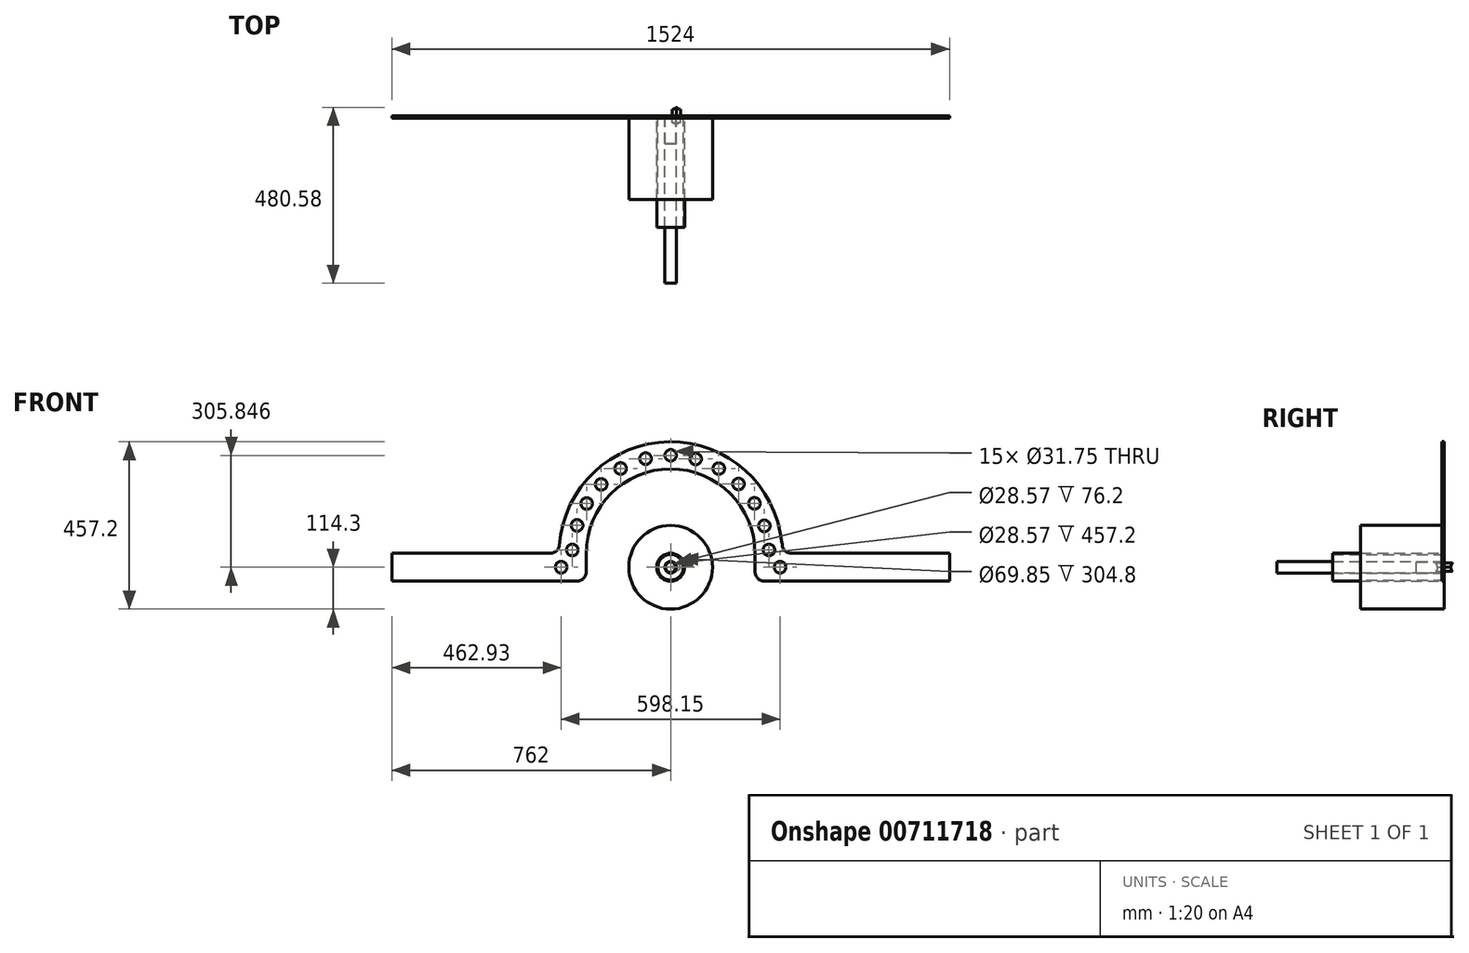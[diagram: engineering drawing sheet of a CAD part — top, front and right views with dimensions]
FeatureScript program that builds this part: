
annotation { "Feature Type Name" : "Feature", "Feature Type Description" : "" }
export const myFeature = defineFeature(function(context is Context, id is Id, definition is map)
    precondition{}
    {
        {
            var Q0;
            Q0=qCreatedBy(makeId("Front.planeOp"),FACE);
            var sketch = newSketch(context, id + "F0", { "sketchPlane" : qUnion([Q0])});
            skLineSegment(sketch, "E0.top", {"start": v(762, -38.1) * mm, "end": v(256.1, -38.1) * mm});
            skLineSegment(sketch, "E0.left", {"start": v(762, 38.1) * mm, "end": v(762, -38.1) * mm});
            skLineSegment(sketch, "E0.right", {"start": v(-762, 38.1) * mm, "end": v(-762, -38.1) * mm});
            skPoint(sketch, "E0.middle", {"position": v(0, 0) * mm});
            skArc(sketch, "E1", {"start": v(303.43, 66.96) * mm, "mid": v(-3.7, 342.88) * mm, "end": v(-304.04, 59.6) * mm});
            skLineSegment(sketch, "E2.trimOffspring", {"start": v(-329.14, 38.1) * mm, "end": v(-762, 38.1) * mm});
            skArc(sketch, "E3", {"start": v(230.7, 38.1) * mm, "mid": v(0, 268.8) * mm, "end": v(-230.7, 38.1) * mm});
            skLineSegment(sketch, "E4.trimOffspring", {"start": v(-256.1, -38.1) * mm, "end": v(-762, -38.1) * mm});
            skLineSegment(sketch, "E5", {"start": v(330.2, 38.1) * mm, "end": v(762, 38.1) * mm});
            skLineSegment(sketch, "E6", {"start": v(230.7, 38.1) * mm, "end": v(230.7, -11.9) * mm});
            skLineSegment(sketch, "E7", {"start": v(-230.7, 38.1) * mm, "end": v(-230.7, -12.7) * mm});
            skLineSegment(sketch, "E8", {"start": v(-303.83, 61.38) * mm, "end": v(-303.74, 63.5) * mm});
            skArc(sketch, "E9", {"start": v(-329.14, 38.1) * mm, "mid": v(-311.18, 45.54) * mm, "end": v(-303.74, 63.5) * mm});
            skPoint(sketch, "E10.orphan", {"position": v(-304.8, 38.1) * mm});
            skArc(sketch, "E11", {"start": v(-256.1, -38.1) * mm, "mid": v(-238.13, -30.66) * mm, "end": v(-230.7, -12.7) * mm});
            skPoint(sketch, "E12.orphan", {"position": v(-230.7, -38.1) * mm});
            skPoint(sketch, "E13.orphan", {"position": v(304.8, 63.5) * mm});
            skPoint(sketch, "E14.orphan", {"position": v(304.8, 38.1) * mm});
            skPoint(sketch, "E15.orphan", {"position": v(230.7, -38.1) * mm});
            skArc(sketch, "E16", {"start": v(304.8, 63.5) * mm, "mid": v(312.24, 45.54) * mm, "end": v(330.2, 38.1) * mm});
            skLineSegment(sketch, "E17", {"start": v(303.43, 66.96) * mm, "end": v(304.8, 63.5) * mm});
            skLineSegment(sketch, "E18", {"start": v(230.7, -11.9) * mm, "end": v(230.7, -12.7) * mm});
            skPoint(sketch, "E19.orphan", {"position": v(190.07, -38.1) * mm});
            skArc(sketch, "E20", {"start": v(230.7, -12.7) * mm, "mid": v(238.13, -30.66) * mm, "end": v(256.1, -38.1) * mm});
            skCircle(sketch, "E21", {"center": v(0, 305.85) * mm, "radius": 15.88 * mm});
            skPoint(sketch, "E22.orphan", {"position": v(0, 342.9) * mm});
            skPoint(sketch, "E23.orphan", {"position": v(0, 268.8) * mm});
            skLineSegment(sketch, "E24", {"start": v(199.2, 268.8) * mm, "end": v(199.2, 268.8) * mm});
            skCircle(sketch, "E25", {"center": v(131.56, 269.72) * mm, "radius": 15.88 * mm});
            skPoint(sketch, "E26.orphan", {"position": v(-268.94, 268.8) * mm});
            skCircle(sketch, "E27", {"center": v(-136.76, 269.9) * mm, "radius": 15.88 * mm});
            skPoint(sketch, "E28.orphan", {"position": v(-200.17, 267.96) * mm});
            skCircle(sketch, "E29", {"center": v(68.39, 295.88) * mm, "radius": 15.88 * mm});
            skCircle(sketch, "E30", {"center": v(-68.38, 296.79) * mm, "radius": 15.88 * mm});
            skCircle(sketch, "E31", {"center": v(-189.65, 226.55) * mm, "radius": 15.88 * mm});
            skCircle(sketch, "E32", {"center": v(185.38, 227.52) * mm, "radius": 15.88 * mm});
            skCircle(sketch, "E33", {"center": v(229.1, 174.63) * mm, "radius": 15.88 * mm});
            skCircle(sketch, "E34", {"center": v(256, 112.9) * mm, "radius": 15.88 * mm});
            skCircle(sketch, "E35", {"center": v(268.64, 47.27) * mm, "radius": 15.88 * mm});
            skCircle(sketch, "E36", {"center": v(299.08, 0) * mm, "radius": 15.88 * mm});
            skCircle(sketch, "E37", {"center": v(-229.36, 174.2) * mm, "radius": 15.88 * mm});
            skCircle(sketch, "E38", {"center": v(-255.6, 114.22) * mm, "radius": 15.88 * mm});
            skCircle(sketch, "E39", {"center": v(-268.64, 47.14) * mm, "radius": 15.88 * mm});
            skCircle(sketch, "E40", {"center": v(-299.07, 0) * mm, "radius": 15.88 * mm});
            skSolve(sketch);
        }
        {
            var Q0;
            Q0 = qSketchRegion(id + "F0", true);
            extrude(context, id + "F1", {"entities" : qUnion([Q0]), "depth" : 6.35 * mm, "offsetDistance" : 25.4 * mm});
        }
        {
            var Q0;
            Q0=qCreatedBy(makeId("Front.planeOp"),FACE);
            var sketch = newSketch(context, id + "F2", { "sketchPlane" : qUnion([Q0])});
            skCircle(sketch, "E41", {"center": v(0, 0) * mm, "radius": 14.29 * mm});
            skCircle(sketch, "E42", {"center": v(0, 0) * mm, "radius": 15.88 * mm});
            skSolve(sketch);
        }
        {
            var Q0;
            Q0 = qSketchRegion(id + "F2", true);
            extrude(context, id + "F3", {"entities" : qUnion([Q0]), "depth" : 76.2 * mm, "offsetDistance" : 25.4 * mm});
        }
        {
            var Q0;
            Q0=qCreatedBy(makeId("Right.planeOp"),FACE);
            var sketch = newSketch(context, id + "F4", { "sketchPlane" : qUnion([Q0])});
            skLineSegment(sketch, "E43.bottom", {"start": v(34.2, 15.88) * mm, "end": v(-34.2, 15.88) * mm});
            skLineSegment(sketch, "E43.top", {"start": v(34.2, -15.88) * mm, "end": v(-34.2, -15.88) * mm});
            skPoint(sketch, "E43.middle", {"position": v(0, 0) * mm});
            skArc(sketch, "E44", {"start": v(34.2, 15.87) * mm, "mid": v(18.32, 0) * mm, "end": v(34.2, -15.88) * mm});
            skArc(sketch, "E45", {"start": v(-34.2, -15.88) * mm, "mid": v(-18.32, 0) * mm, "end": v(-34.2, 15.88) * mm});
            skSolve(sketch);
        }
        {
            var Q0;
            Q0 = qSketchRegion(id + "F4", true);
            extrude(context, id + "F5", {"entities" : qUnion([Q0]), "depth" : 31.75 * mm, "offsetDistance" : 25.4 * mm});
        }
        {
            var Q0;
            Q0=makeQuery(id+"F5.opExtrude","CAP_EDGE",EDGE,{"disambiguationData":[OSD([sQuery(id+"F4.wireOp",EDGE,"E43.bottom")])],"isStart":false});
            var Q1;
            Q1=makeQuery(id+"F5.opExtrude","CAP_EDGE",EDGE,{"disambiguationData":[OSD([sQuery(id+"F4.wireOp",EDGE,"E43.bottom")])],"isStart":true});
            var Q2;
            Q2=makeQuery(id+"F5.opExtrude","CAP_EDGE",EDGE,{"disambiguationData":[OSD([sQuery(id+"F4.wireOp",EDGE,"E43.top")])],"isStart":true});
            var Q3;
            Q3=makeQuery(id+"F5.opExtrude","CAP_EDGE",EDGE,{"disambiguationData":[OSD([sQuery(id+"F4.wireOp",EDGE,"E43.top")])],"isStart":false});
            fillet(context, id + "F6", {"entities" : qUnion([Q0, Q1, Q2, Q3]), "radius" : 31.75 * mm, "tangentPropagation" : true, "allowEdgeOverflow" : false});
        }
        {
            var Q0;
            Q0=qCreatedBy(makeId("Front.planeOp"),FACE);
            var sketch = newSketch(context, id + "F7", { "sketchPlane" : qUnion([Q0])});
            skCircle(sketch, "E46", {"center": v(0, 0) * mm, "radius": 15.88 * mm});
            skCircle(sketch, "E47", {"center": v(0, 0) * mm, "radius": 14.29 * mm});
            skSolve(sketch);
        }
        {
            var Q0;
            Q0 = qSketchRegion(id + "F7", true);
            extrude(context, id + "F8", {"entities" : qUnion([Q0]), "depth" : 457.2 * mm, "offsetDistance" : 25.4 * mm});
        }
        {
            var Q0;
            Q0=qCreatedBy(makeId("Front.planeOp"),FACE);
            var sketch = newSketch(context, id + "F9", { "sketchPlane" : qUnion([Q0])});
            skCircle(sketch, "E48", {"center": v(0, 0) * mm, "radius": 114.3 * mm});
            skSolve(sketch);
        }
        {
            var Q0;
            Q0 = qSketchRegion(id + "F9", true);
            extrude(context, id + "F10", {"entities" : qUnion([Q0]), "depth" : 228.6 * mm, "offsetDistance" : 25.4 * mm});
        }
        {
            var Q0;
            Q0=qCreatedBy(makeId("Front.planeOp"),FACE);
            var sketch = newSketch(context, id + "F11", { "sketchPlane" : qUnion([Q0])});
            skCircle(sketch, "E49", {"center": v(0, 0) * mm, "radius": 38.1 * mm});
            skCircle(sketch, "E50", {"center": v(0, 0) * mm, "radius": 34.93 * mm});
            skSolve(sketch);
        }
        {
            var Q0;
            Q0 = qSketchRegion(id + "F11", true);
            extrude(context, id + "F12", {"entities" : qUnion([Q0]), "depth" : 304.8 * mm, "offsetDistance" : 25.4 * mm});
        }
    });
